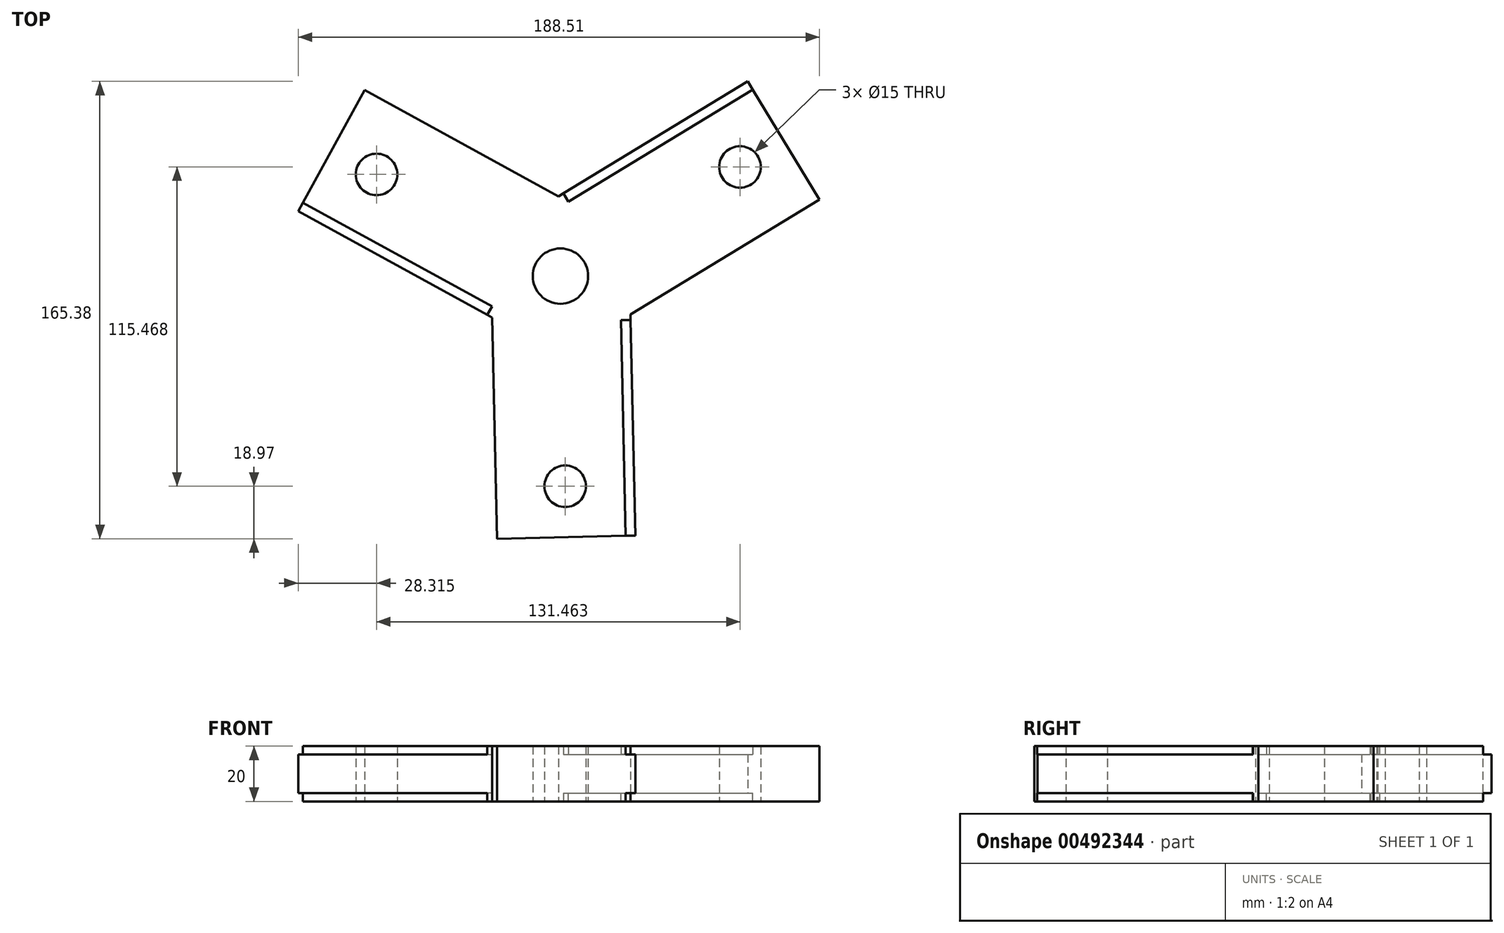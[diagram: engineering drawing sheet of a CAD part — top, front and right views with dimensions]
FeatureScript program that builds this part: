
annotation { "Feature Type Name" : "Feature", "Feature Type Description" : "" }
export const myFeature = defineFeature(function(context is Context, id is Id, definition is map)
    precondition{}
    {
        {
            var Q0;
            Q0=qCreatedBy(makeId("Top.planeOp"),FACE);
            var sketch = newSketch(context, id + "F0", { "sketchPlane" : qUnion([Q0])});
            skCircle(sketch, "E0", {"center": v(0, 0) * mm, "radius": 10 * mm});
            skCircle(sketch, "E1.cCircle", {"center": v(0, 0) * mm, "radius": 14.43 * mm, "construction": true});
            skLineSegment(sketch, "E1.0", {"start": v(-0.65, 28.86) * mm, "end": v(25.32, -13.87) * mm});
            skLineSegment(sketch, "E1.1", {"start": v(25.32, -13.87) * mm, "end": v(-24.67, -15) * mm});
            skLineSegment(sketch, "E1.2", {"start": v(-24.67, -15) * mm, "end": v(-0.65, 28.86) * mm});
            skPoint(sketch, "E1.0.midPoint", {"position": v(12.33, 7.5) * mm});
            skLineSegment(sketch, "E2", {"start": v(-0.65, 28.86) * mm, "end": v(-70.81, 67.3) * mm});
            skLineSegment(sketch, "E3", {"start": v(-24.67, -15) * mm, "end": v(-94.83, 23.44) * mm});
            skLineSegment(sketch, "E4", {"start": v(-70.81, 67.3) * mm, "end": v(-94.83, 23.44) * mm});
            skLineSegment(sketch, "E5", {"start": v(-24.67, -15) * mm, "end": v(-22.87, -94.97) * mm});
            skLineSegment(sketch, "E6", {"start": v(25.32, -13.87) * mm, "end": v(27.11, -93.85) * mm});
            skLineSegment(sketch, "E7", {"start": v(27.11, -93.85) * mm, "end": v(-22.87, -94.97) * mm});
            skLineSegment(sketch, "E8", {"start": v(-0.65, 28.86) * mm, "end": v(67.72, 70.4) * mm});
            skLineSegment(sketch, "E9", {"start": v(25.32, -13.87) * mm, "end": v(93.68, 27.68) * mm});
            skLineSegment(sketch, "E10", {"start": v(67.72, 70.4) * mm, "end": v(93.68, 27.68) * mm});
            skCircle(sketch, "E11", {"center": v(-66.51, 36.77) * mm, "radius": 7.5 * mm});
            skLineSegment(sketch, "E12", {"start": v(-70.81, 67.3) * mm, "end": v(-82.82, 45.37) * mm});
            skLineSegment(sketch, "E13", {"start": v(-82.82, 45.37) * mm, "end": v(0, 0) * mm});
            skLineSegment(sketch, "E14", {"start": v(0, 0) * mm, "end": v(80.7, 49.04) * mm});
            skLineSegment(sketch, "E15", {"start": v(0, 0) * mm, "end": v(2.12, -94.4) * mm});
            skCircle(sketch, "E16", {"center": v(1.7, -76) * mm, "radius": 7.5 * mm});
            skCircle(sketch, "E17", {"center": v(64.95, 39.47) * mm, "radius": 7.5 * mm});
            skSolve(sketch);
        }
        {
            var Q0;
            {var subQ6=sQuery(id+"F0.wireOp",EDGE,"E9");Q0=makeQuery(id+"F0.imprint","IMPRINT",FACE,{"disambiguationData":[TD([[makeQuery(id+"F0.imprint","IMPRINT",EDGE,{"derivedFrom":subQ6}),1.0]])]});}
            var Q1;
            {var subQ5=sQuery(id+"F0.wireOp",EDGE,"E8");Q1=makeQuery(id+"F0.imprint","IMPRINT",FACE,{"disambiguationData":[TD([[makeQuery(id+"F0.imprint","IMPRINT",EDGE,{"derivedFrom":subQ5}),-1.0]])]});}
            var Q2;
            {var subQ5=sQuery(id+"F0.wireOp",EDGE,"E3");Q2=makeQuery(id+"F0.imprint","IMPRINT",FACE,{"disambiguationData":[TD([[makeQuery(id+"F0.imprint","IMPRINT",EDGE,{"derivedFrom":subQ5}),-1.0]])]});}
            var Q3;
            {var subQ6=sQuery(id+"F0.wireOp",EDGE,"E5");Q3=makeQuery(id+"F0.imprint","IMPRINT",FACE,{"disambiguationData":[TD([[makeQuery(id+"F0.imprint","IMPRINT",EDGE,{"derivedFrom":subQ6}),1.0]])]});}
            var Q4;
            {var subQ1=sQuery(id+"F0.wireOp",EDGE,"E6");Q4=makeQuery(id+"F0.imprint","IMPRINT",FACE,{"disambiguationData":[TD([[makeQuery(id+"F0.imprint","IMPRINT",EDGE,{"derivedFrom":subQ1}),-1.0]])]});}
            var Q5;
            {var subQ5=sQuery(id+"F0.wireOp",EDGE,"E2");Q5=makeQuery(id+"F0.imprint","IMPRINT",FACE,{"disambiguationData":[TD([[makeQuery(id+"F0.imprint","IMPRINT",EDGE,{"derivedFrom":subQ5}),1.0]])]});}
            var Q6;
            {var subQ3=sQuery(id+"F0.wireOp",EDGE,"E13");var subQ5=sQuery(id+"F0.wireOp",EDGE,"E0");var subQ6=makeQuery(id+"F0.imprint","INTERSECT",VERTEX,{"derivedFrom":[subQ5,subQ3]});Q6=makeQuery(id+"F0.imprint","IMPRINT",FACE,{"disambiguationData":[TD([[makeQuery(id+"F0.imprint","IMPRINT",EDGE,{"disambiguationData":[TD([[subQ6,-1.0]])],"derivedFrom":subQ5}),-1.0]])]});}
            var Q7;
            {var subQ0=sQuery(id+"F0.wireOp",EDGE,"E13");var subQ1=sQuery(id+"F0.wireOp",EDGE,"E0");var subQ2=makeQuery(id+"F0.imprint","INTERSECT",VERTEX,{"derivedFrom":[subQ1,subQ0]});Q7=makeQuery(id+"F0.imprint","IMPRINT",FACE,{"disambiguationData":[TD([[makeQuery(id+"F0.imprint","IMPRINT",EDGE,{"disambiguationData":[TD([[subQ2,1.0]])],"derivedFrom":subQ1}),-1.0]])]});}
            var Q8;
            {var subQ5=sQuery(id+"F0.wireOp",EDGE,"E14");var subQ6=sQuery(id+"F0.wireOp",EDGE,"E0");var subQ7=makeQuery(id+"F0.imprint","INTERSECT",VERTEX,{"derivedFrom":[subQ6,subQ5]});Q8=makeQuery(id+"F0.imprint","IMPRINT",FACE,{"disambiguationData":[TD([[makeQuery(id+"F0.imprint","IMPRINT",EDGE,{"disambiguationData":[TD([[subQ7,1.0]])],"derivedFrom":subQ6}),-1.0]])]});}
            extrude(context, id + "F1", {"entities" : qUnion([Q0, Q1, Q2, Q3, Q4, Q5, Q6, Q7, Q8]), "depth" : 20 * mm});
        }
        {
            var Q0;
            Q0=makeQuery(id+"F1.opExtrude","SWEPT_FACE",FACE,{"disambiguationData":[OSD([sQuery(id+"F0.wireOp",EDGE,"E4"),sQuery(id+"F0.wireOp",EDGE,"E12")])]});
            var sketch = newSketch(context, id + "F2", { "sketchPlane" : qUnion([Q0])});
            skLineSegment(sketch, "E18.bottom", {"start": v(25, 20) * mm, "end": v(21.5, 20) * mm});
            skLineSegment(sketch, "E18.top", {"start": v(25, 17) * mm, "end": v(21.5, 17) * mm});
            skLineSegment(sketch, "E18.left", {"start": v(25, 20) * mm, "end": v(25, 17) * mm});
            skLineSegment(sketch, "E18.right", {"start": v(21.5, 20) * mm, "end": v(21.5, 17) * mm});
            skLineSegment(sketch, "E19.bottom", {"start": v(25, 0) * mm, "end": v(21.5, 0) * mm});
            skLineSegment(sketch, "E19.top", {"start": v(25, 3) * mm, "end": v(21.5, 3) * mm});
            skLineSegment(sketch, "E19.left", {"start": v(25, 0) * mm, "end": v(25, 3) * mm});
            skLineSegment(sketch, "E19.right", {"start": v(21.5, 0) * mm, "end": v(21.5, 3) * mm});
            skSolve(sketch);
        }
        {
            var Q0;
            Q0=makeQuery(id+"F2.imprint","IMPRINT",FACE,{"disambiguationData":[TD([[makeQuery(id+"F2.imprint","IMPRINT",EDGE,{"derivedFrom":sQuery(id+"F2.wireOp",EDGE,"E18.bottom")}),-1.0]])]});
            var Q1;
            Q1=makeQuery(id+"F2.imprint","IMPRINT",FACE,{"disambiguationData":[TD([[makeQuery(id+"F2.imprint","IMPRINT",EDGE,{"derivedFrom":sQuery(id+"F2.wireOp",EDGE,"E19.bottom")}),1.0]])]});
            extrude(context, id + "F3", {"entities" : qUnion([Q0, Q1]), "operationType" : NewBodyOperationType.REMOVE, "oppositeDirection" : true, "depth" : 78 * mm});
        }
        {
            var Q0;
            Q0=makeQuery(id+"F1.opExtrude","SWEPT_FACE",FACE,{"disambiguationData":[OSD([sQuery(id+"F0.wireOp",EDGE,"E7")])]});
            var sketch = newSketch(context, id + "F4", { "sketchPlane" : qUnion([Q0])});
            skLineSegment(sketch, "E20.bottom", {"start": v(25, 20) * mm, "end": v(21.5, 20) * mm});
            skLineSegment(sketch, "E20.top", {"start": v(25, 17) * mm, "end": v(21.5, 17) * mm});
            skLineSegment(sketch, "E20.left", {"start": v(25, 20) * mm, "end": v(25, 17) * mm});
            skLineSegment(sketch, "E20.right", {"start": v(21.5, 20) * mm, "end": v(21.5, 17) * mm});
            skLineSegment(sketch, "E21.bottom", {"start": v(25, 0) * mm, "end": v(21.5, 0) * mm});
            skLineSegment(sketch, "E21.top", {"start": v(25, 3) * mm, "end": v(21.5, 3) * mm});
            skLineSegment(sketch, "E21.left", {"start": v(25, 0) * mm, "end": v(25, 3) * mm});
            skLineSegment(sketch, "E21.right", {"start": v(21.5, 0) * mm, "end": v(21.5, 3) * mm});
            skSolve(sketch);
        }
        {
            var Q0;
            Q0=makeQuery(id+"F4.imprint","IMPRINT",FACE,{"disambiguationData":[TD([[makeQuery(id+"F4.imprint","IMPRINT",EDGE,{"derivedFrom":sQuery(id+"F4.wireOp",EDGE,"E20.bottom")}),1.0]])]});
            var Q1;
            Q1=makeQuery(id+"F4.imprint","IMPRINT",FACE,{"disambiguationData":[TD([[makeQuery(id+"F4.imprint","IMPRINT",EDGE,{"derivedFrom":sQuery(id+"F4.wireOp",EDGE,"E21.bottom")}),-1.0]])]});
            extrude(context, id + "F5", {"entities" : qUnion([Q0, Q1]), "operationType" : NewBodyOperationType.REMOVE, "oppositeDirection" : true, "depth" : 78 * mm});
        }
        {
            var Q0;
            Q0=makeQuery(id+"F1.opExtrude","SWEPT_FACE",FACE,{"disambiguationData":[OSD([sQuery(id+"F0.wireOp",EDGE,"E10")])]});
            var sketch = newSketch(context, id + "F6", { "sketchPlane" : qUnion([Q0])});
            skLineSegment(sketch, "E22.bottom", {"start": v(25, 20) * mm, "end": v(21.5, 20) * mm});
            skLineSegment(sketch, "E22.top", {"start": v(25, 17) * mm, "end": v(21.5, 17) * mm});
            skLineSegment(sketch, "E22.left", {"start": v(25, 20) * mm, "end": v(25, 17) * mm});
            skLineSegment(sketch, "E22.right", {"start": v(21.5, 20) * mm, "end": v(21.5, 17) * mm});
            skLineSegment(sketch, "E23.bottom", {"start": v(25, 0) * mm, "end": v(21.5, 0) * mm});
            skLineSegment(sketch, "E23.top", {"start": v(25, 3) * mm, "end": v(21.5, 3) * mm});
            skLineSegment(sketch, "E23.left", {"start": v(25, 0) * mm, "end": v(25, 3) * mm});
            skLineSegment(sketch, "E23.right", {"start": v(21.5, 0) * mm, "end": v(21.5, 3) * mm});
            skSolve(sketch);
        }
        {
            var Q0;
            Q0=makeQuery(id+"F6.imprint","IMPRINT",FACE,{"disambiguationData":[TD([[makeQuery(id+"F6.imprint","IMPRINT",EDGE,{"derivedFrom":sQuery(id+"F6.wireOp",EDGE,"E22.bottom")}),1.0]])]});
            var Q1;
            Q1=makeQuery(id+"F6.imprint","IMPRINT",FACE,{"disambiguationData":[TD([[makeQuery(id+"F6.imprint","IMPRINT",EDGE,{"derivedFrom":sQuery(id+"F6.wireOp",EDGE,"E23.bottom")}),-1.0]])]});
            extrude(context, id + "F7", {"entities" : qUnion([Q0, Q1]), "operationType" : NewBodyOperationType.REMOVE, "oppositeDirection" : true, "depth" : 78 * mm});
        }
    });
